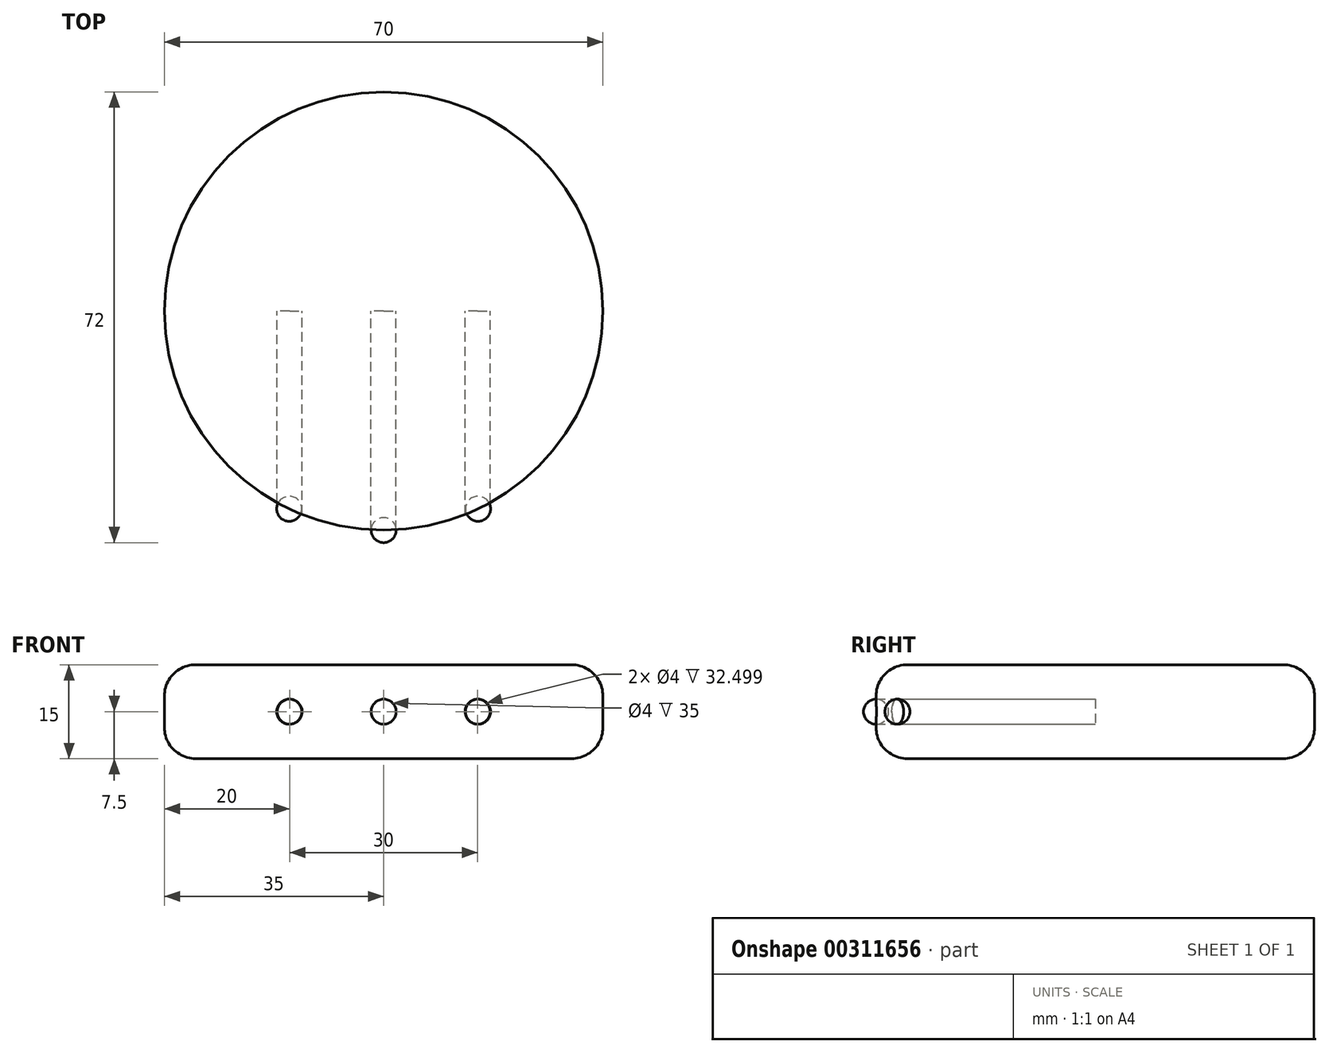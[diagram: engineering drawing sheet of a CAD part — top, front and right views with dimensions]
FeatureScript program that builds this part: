
annotation { "Feature Type Name" : "Feature", "Feature Type Description" : "" }
export const myFeature = defineFeature(function(context is Context, id is Id, definition is map)
    precondition{}
    {
        {
            var Q0;
            Q0=qCreatedBy(makeId("Front.planeOp"),FACE);
            var sketch = newSketch(context, id + "F0", { "sketchPlane" : qUnion([Q0])});
            skLineSegment(sketch, "E0", {"start": v(0, 0) * mm, "end": v(0, 41.17) * mm, "construction": true});
            skLineSegment(sketch, "E1", {"start": v(35, 10) * mm, "end": v(35, 5) * mm});
            skLineSegment(sketch, "E2", {"start": v(30, 15) * mm, "end": v(0, 15) * mm});
            skPoint(sketch, "E3.orphan", {"position": v(35, 5) * mm});
            skLineSegment(sketch, "E4", {"start": v(0, 0) * mm, "end": v(30, 0) * mm});
            skPoint(sketch, "E5.visualSharp", {"position": v(35, 0) * mm});
            skArc(sketch, "E5.filletArc", {"start": v(30, 0) * mm, "mid": v(33.54, 1.46) * mm, "end": v(35, 5) * mm});
            skPoint(sketch, "E6.visualSharp", {"position": v(35, 15) * mm});
            skArc(sketch, "E6.filletArc", {"start": v(35, 10) * mm, "mid": v(33.54, 13.54) * mm, "end": v(30, 15) * mm});
            skLineSegment(sketch, "E7", {"start": v(0, 15) * mm, "end": v(0, 0) * mm});
            skSolve(sketch);
        }
        {
            var Q0;
            Q0 = qSketchRegion(id + "F0", true);
            var Q1;
            Q1=sQuery(id+"F0.wireOp",EDGE,"E7");
            revolve(context, id + "F1", {"entities" : qUnion([Q0]), "axis" : qUnion([Q1]), "revolveType" : RevolveType.FULL});
        }
        {
            var Q0;
            Q0=qCreatedBy(makeId("Front.planeOp"),FACE);
            var sketch = newSketch(context, id + "F2", { "sketchPlane" : qUnion([Q0])});
            skLineSegment(sketch, "E8.0", {"start": v(-35, 10) * mm, "end": v(35, 10) * mm, "construction": true});
            skLineSegment(sketch, "E9.0", {"start": v(-35, 5) * mm, "end": v(35, 5) * mm, "construction": true});
            skLineSegment(sketch, "E10", {"start": v(0, 10) * mm, "end": v(0, 5) * mm, "construction": true});
            skCircle(sketch, "E11", {"center": v(0, 7.5) * mm, "radius": 2 * mm});
            skCircle(sketch, "E12", {"center": v(-15, 7.5) * mm, "radius": 2 * mm});
            skCircle(sketch, "E13", {"center": v(15, 7.5) * mm, "radius": 2 * mm});
            skSolve(sketch);
        }
        {
            var Q0;
            Q0 = qSketchRegion(id + "F2", true);
            extrude(context, id + "F3", {"entities" : qUnion([Q0]), "operationType" : NewBodyOperationType.REMOVE, "endBound" : BoundingType.THROUGH_ALL, "depth" : 25 * mm});
        }
        {
            var Q0;
            Q0=qCreatedBy(makeId("Right.planeOp"),FACE);
            var sketch = newSketch(context, id + "F4", { "sketchPlane" : qUnion([Q0])});
            skLineSegment(sketch, "E14", {"start": v(-35, 9.5) * mm, "end": v(-35, 5.5) * mm});
            skLineSegment(sketch, "E15", {"start": v(-35, 7.5) * mm, "end": v(-36.11, 7.5) * mm, "construction": true});
            skArc(sketch, "E16", {"start": v(-35, 9.5) * mm, "mid": v(-37, 7.5) * mm, "end": v(-35, 5.5) * mm});
            skSolve(sketch);
        }
        {
            var Q0;
            Q0 = qSketchRegion(id + "F4", true);
            var Q1;
            Q1=sQuery(id+"F4.wireOp",EDGE,"E14");
            revolve(context, id + "F5", {"entities" : qUnion([Q0]), "axis" : qUnion([Q1]), "revolveType" : RevolveType.FULL});
        }
        {
            var Q0;
            Q0=makeQuery(id+"F5.opRevolve","SWEPT_BODY",BODY,{"disambiguationData":[OSD([sQuery(id+"F4.wireOp",EDGE,"E14"),sQuery(id+"F4.wireOp",EDGE,"E16")])]});
            var Q1;
            Q1=makeQuery(id+"F1.opRevolve","SWEPT_FACE",FACE,{"disambiguationData":[OSD([sQuery(id+"F0.wireOp",EDGE,"E1")])]});
            circularPattern(context, id + "F6", {"entities" : qUnion([Q0]), "axis" : qUnion([Q1]), "angle" : 25.5 * degree, "instanceCount" : 2, "equalSpace" : true});
        }
        {
            var Q0;
            Q0=makeQuery(id+"F6.opPattern","COPY",BODY,{"derivedFrom":makeQuery(id+"F5.opRevolve","SWEPT_BODY",BODY,{"disambiguationData":[OSD([sQuery(id+"F4.wireOp",EDGE,"E14"),sQuery(id+"F4.wireOp",EDGE,"E16")])]}),"instanceName":"1"});
            var Q1;
            Q1=qCreatedBy(makeId("Right.planeOp"),FACE);
            mirror(context, id + "F7", {"entities" : qUnion([Q0]), "mirrorPlane" : qUnion([Q1])});
        }
    });
